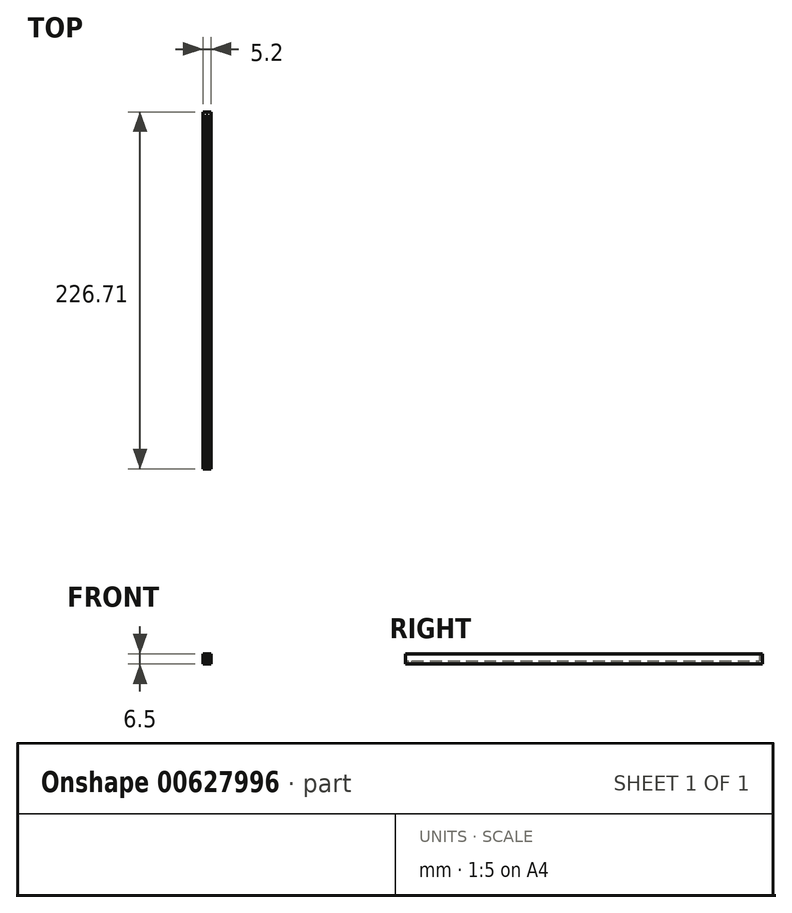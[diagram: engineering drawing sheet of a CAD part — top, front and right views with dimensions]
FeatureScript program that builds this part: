
annotation { "Feature Type Name" : "Feature", "Feature Type Description" : "" }
export const myFeature = defineFeature(function(context is Context, id is Id, definition is map)
    precondition{}
    {
        {
            var Q0;
            Q0=qCreatedBy(makeId("Top.planeOp"),FACE);
            var sketch = newSketch(context, id + "F0", { "sketchPlane" : qUnion([Q0])});
            skLineSegment(sketch, "E0.bottom", {"start": v(0, 0) * mm, "end": v(5.2, 0) * mm});
            skLineSegment(sketch, "E0.top", {"start": v(0, 226.71) * mm, "end": v(5.2, 226.71) * mm});
            skLineSegment(sketch, "E0.left", {"start": v(0, 0) * mm, "end": v(0, 226.71) * mm});
            skLineSegment(sketch, "E0.right", {"start": v(5.2, 0) * mm, "end": v(5.2, 226.71) * mm});
            skSolve(sketch);
        }
        {
            var Q0;
            Q0=makeQuery(id+"F0.imprint","IMPRINT",FACE,{"disambiguationData":[TD([[makeQuery(id+"F0.imprint","IMPRINT",EDGE,{"derivedFrom":sQuery(id+"F0.wireOp",EDGE,"E0.bottom")}),1.0]])]});
            extrude(context, id + "F1", {"entities" : qUnion([Q0]), "depth" : 2 * mm, "offsetDistance" : 25 * mm});
        }
        {
            var Q0;
            Q0=makeQuery(id+"F1.opExtrude","CAP_FACE",FACE,{"disambiguationData":[OSD([sQuery(id+"F0.wireOp",EDGE,"E0.bottom"),sQuery(id+"F0.wireOp",EDGE,"E0.top"),sQuery(id+"F0.wireOp",EDGE,"E0.left"),sQuery(id+"F0.wireOp",EDGE,"E0.right")])],"isStart":false});
            var sketch = newSketch(context, id + "F2", { "sketchPlane" : qUnion([Q0])});
            skLineSegment(sketch, "E1.bottom", {"start": v(0, 0) * mm, "end": v(2, 0) * mm});
            skLineSegment(sketch, "E1.top", {"start": v(0, 226.71) * mm, "end": v(5.2, 226.71) * mm});
            skLineSegment(sketch, "E1.left", {"start": v(0, 0) * mm, "end": v(0, 226.71) * mm});
            skLineSegment(sketch, "E1.right", {"start": v(5.2, 0) * mm, "end": v(5.2, 226.71) * mm});
            skLineSegment(sketch, "E2.top", {"start": v(2, 224.71) * mm, "end": v(3.2, 224.71) * mm});
            skLineSegment(sketch, "E2.left", {"start": v(2, 0) * mm, "end": v(2, 224.71) * mm});
            skLineSegment(sketch, "E2.right", {"start": v(3.2, 0) * mm, "end": v(3.2, 224.71) * mm});
            skLineSegment(sketch, "E3.trimOffspring", {"start": v(3.2, 0) * mm, "end": v(5.2, 0) * mm});
            skSolve(sketch);
        }
        {
            var Q0;
            Q0=makeQuery(id+"F2.imprint","IMPRINT",FACE,{"disambiguationData":[TD([[makeQuery(id+"F2.imprint","IMPRINT",EDGE,{"derivedFrom":sQuery(id+"F2.wireOp",EDGE,"E1.bottom")}),1.0]])]});
            extrude(context, id + "F3", {"entities" : qUnion([Q0]), "operationType" : NewBodyOperationType.ADD, "depth" : 4.5 * mm, "offsetDistance" : 25 * mm});
        }
        {
            var Q0;
            Q0=makeQuery(id+"F1.opExtrude","CAP_FACE",FACE,{"disambiguationData":[OSD([sQuery(id+"F0.wireOp",EDGE,"E0.bottom"),sQuery(id+"F0.wireOp",EDGE,"E0.top"),sQuery(id+"F0.wireOp",EDGE,"E0.left"),sQuery(id+"F0.wireOp",EDGE,"E0.right")])],"isStart":false});
            var sketch = newSketch(context, id + "F4", { "sketchPlane" : qUnion([Q0])});
            skLineSegment(sketch, "E4.bottom", {"start": v(2, 1.9) * mm, "end": v(3.2, 1.9) * mm});
            skLineSegment(sketch, "E4.top", {"start": v(2, 4) * mm, "end": v(3.2, 4) * mm});
            skLineSegment(sketch, "E4.left", {"start": v(2, 1.9) * mm, "end": v(2, 4) * mm});
            skLineSegment(sketch, "E4.right", {"start": v(3.2, 1.9) * mm, "end": v(3.2, 4) * mm});
            skSolve(sketch);
        }
        {
            var Q0;
            Q0=makeQuery(id+"F4.imprint","IMPRINT",FACE,{"disambiguationData":[TD([[makeQuery(id+"F4.imprint","IMPRINT",EDGE,{"derivedFrom":sQuery(id+"F4.wireOp",EDGE,"E4.bottom")}),1.0]])]});
            extrude(context, id + "F5", {"entities" : qUnion([Q0]), "operationType" : NewBodyOperationType.REMOVE, "oppositeDirection" : true, "depth" : 25 * mm, "offsetDistance" : 25 * mm});
        }
        {
            var Q0;
            Q0=makeQuery(id+"F1.opExtrude","CAP_EDGE",EDGE,{"disambiguationData":[OSD([sQuery(id+"F0.wireOp",EDGE,"E0.bottom")])],"isStart":false});
            chamfer(context, id + "F6", {"entities" : qUnion([Q0]), "width" : 1 * mm, "tangentPropagation" : true});
        }
    });
